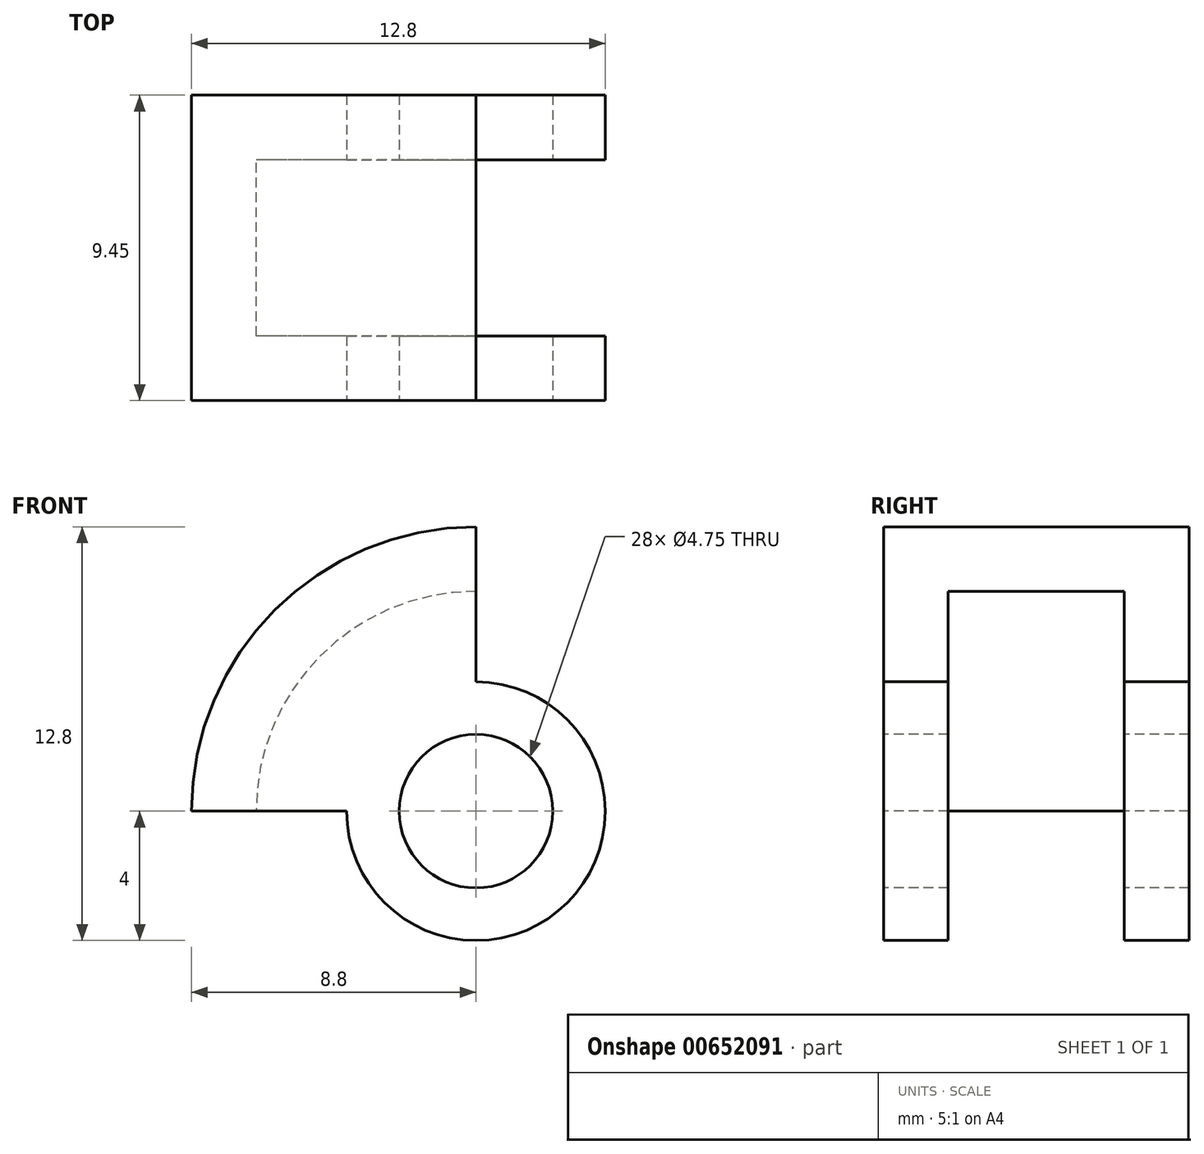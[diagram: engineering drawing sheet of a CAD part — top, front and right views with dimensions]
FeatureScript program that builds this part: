
annotation { "Feature Type Name" : "Feature", "Feature Type Description" : "" }
export const myFeature = defineFeature(function(context is Context, id is Id, definition is map)
    precondition{}
    {
        {
            var Q0;
            Q0=qCreatedBy(makeId("Front.planeOp"),FACE);
            var sketch = newSketch(context, id + "F0", { "sketchPlane" : qUnion([Q0])});
            skCircle(sketch, "E0", {"center": v(0, 0) * mm, "radius": 8.8 * mm});
            skSolve(sketch);
        }
        {
            var Q0;
            Q0=makeQuery(id+"F0.imprint","IMPRINT",FACE,{"disambiguationData":[TD([[makeQuery(id+"F0.imprint","IMPRINT",EDGE,{"derivedFrom":sQuery(id+"F0.wireOp",EDGE,"E0")}),1.0]])]});
            extrude(context, id + "F1", {"entities" : qUnion([Q0]), "depth" : 9.45 * mm, "offsetDistance" : 25 * mm});
        }
        {
            var Q0;
            Q0=makeQuery(id+"F1.opExtrude","CAP_FACE",FACE,{"disambiguationData":[OSD([sQuery(id+"F0.wireOp",EDGE,"E0")])],"isStart":false});
            var sketch = newSketch(context, id + "F2", { "sketchPlane" : qUnion([Q0])});
            skCircle(sketch, "E1", {"center": v(0, 0) * mm, "radius": 4 * mm});
            skLineSegment(sketch, "E2", {"start": v(0, 0) * mm, "end": v(-8.8, 0) * mm});
            skLineSegment(sketch, "E3", {"start": v(0, 0) * mm, "end": v(0, 8.8) * mm});
            skCircle(sketch, "E4", {"center": v(0, 0) * mm, "radius": 2.38 * mm});
            skSolve(sketch);
        }
        {
            var Q0;
            {var subQ0=sQuery(id+"F2.wireOp",EDGE,"E2");var subQ1=sQuery(id+"F2.wireOp",EDGE,"E1");var subQ2=makeQuery(id+"F2.imprint","INTERSECT",VERTEX,{"derivedFrom":[subQ1,subQ0]});Q0=makeQuery(id+"F2.imprint","IMPRINT",FACE,{"disambiguationData":[TD([[makeQuery(id+"F2.imprint","IMPRINT",EDGE,{"disambiguationData":[TD([[subQ2,-1.0]])],"derivedFrom":subQ1}),-1.0]])]});}
            extrude(context, id + "F3", {"entities" : qUnion([Q0]), "operationType" : NewBodyOperationType.REMOVE, "oppositeDirection" : true, "depth" : 25 * mm});
        }
        {
            var Q0;
            Q0=makeQuery(id+"F3.boolean.opBoolean","COPY",FACE,{"derivedFrom":makeQuery(id+"F3.opExtrude","SWEPT_FACE",FACE,{"disambiguationData":[OSD([sQuery(id+"F2.wireOp",EDGE,"E2")])]})});
            var Q1;
            Q1=makeQuery(id+"F3.boolean.opBoolean","COPY",FACE,{"derivedFrom":makeQuery(id+"F3.opExtrude","SWEPT_FACE",FACE,{"disambiguationData":[OSD([sQuery(id+"F2.wireOp",EDGE,"E1")])]})});
            var Q2;
            Q2=makeQuery(id+"F3.boolean.opBoolean","COPY",FACE,{"derivedFrom":makeQuery(id+"F3.opExtrude","SWEPT_FACE",FACE,{"disambiguationData":[OSD([sQuery(id+"F2.wireOp",EDGE,"E3")])]})});
            shell(context, id + "F4", {"entities" : qUnion([Q0, Q1, Q2]), "thickness" : 2 * mm});
        }
        {
            var Q0;
            {var subQ0=sQuery(id+"F2.wireOp",EDGE,"E3");var subQ1=sQuery(id+"F2.wireOp",EDGE,"E2");var subQ2=makeQuery(id+"F2.imprint","INTERSECT",VERTEX,{"derivedFrom":[subQ1,subQ0]});Q0=makeQuery(id+"F2.imprint","IMPRINT",FACE,{"disambiguationData":[TD([[makeQuery(id+"F2.imprint","IMPRINT",EDGE,{"disambiguationData":[TD([[subQ2,-1.0]])],"derivedFrom":subQ1}),1.0]])]});}
            var Q1;
            {var subQ0=sQuery(id+"F2.wireOp",EDGE,"E3");var subQ1=sQuery(id+"F2.wireOp",EDGE,"E2");var subQ2=makeQuery(id+"F2.imprint","INTERSECT",VERTEX,{"derivedFrom":[subQ1,subQ0]});Q1=makeQuery(id+"F2.imprint","IMPRINT",FACE,{"disambiguationData":[TD([[makeQuery(id+"F2.imprint","IMPRINT",EDGE,{"disambiguationData":[TD([[subQ2,-1.0]])],"derivedFrom":subQ1}),-1.0]])]});}
            extrude(context, id + "F5", {"entities" : qUnion([Q0, Q1]), "operationType" : NewBodyOperationType.REMOVE, "oppositeDirection" : true, "depth" : 25 * mm});
        }
    });
